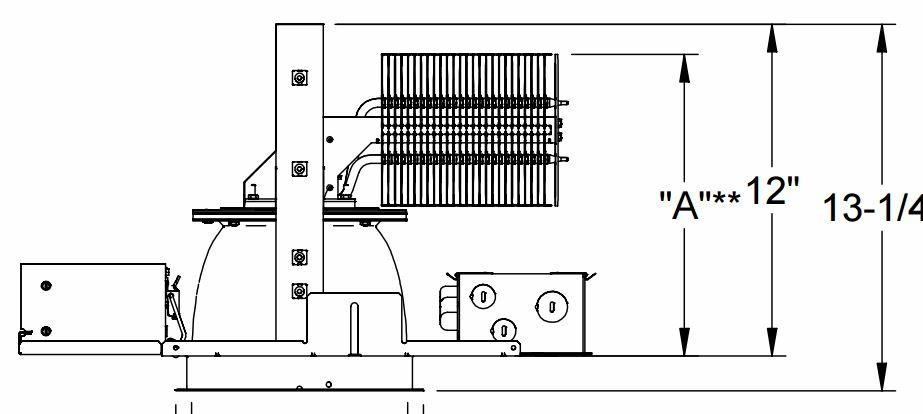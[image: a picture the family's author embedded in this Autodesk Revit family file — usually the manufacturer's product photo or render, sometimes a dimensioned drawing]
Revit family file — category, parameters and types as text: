
# Revit family: MD8LED Downlight
name_source: partatom
category: Lighting Fixtures
units: mm (PartAtom-declared; Revit-internal decimal feet)

## family parameters
Cut with Voids When Loaded = No
Host = Face
Light Source = Yes
OmniClass Number = 23.80.70.11
OmniClass Title = Luminaries for Internal Lighting
Part Type = Normal
Room Calculation Point = No
Round Connector Dimension = Use Diameter
Shared = No

## types (1)
- MD8LED
    Apparent Load = 57 VA
    Color Filter = 16777215
    Default Elevation = 8 1/4"
    Description = High-output LED downlight delivering more than 16,500 lumens suitable for the large commercial and architectural interiors
    Dimming Lamp Color Temperature Shift = <None>
    Emit Shape Visible in Rendering = No
    Emit from Circle Diameter = 7"
    Finish = Black
    Glass = Glass
    Housing = Reflector
    Lamp = One
    Manufacturer = Prescolite
    Model = MD8LED
    Photometric Web File = MD8LED12L35K8 8MD12LFL35.IES
    Tilt Angle = -90.00°
    URL = https://www.currentlighting.com
    Warranty = 5 Years Warranty
    Wattage Comments = 57W

## geometry (parser evidence)
native form markers: Blend x1, Sweep x5
no freeform markers — native parametric forms only
